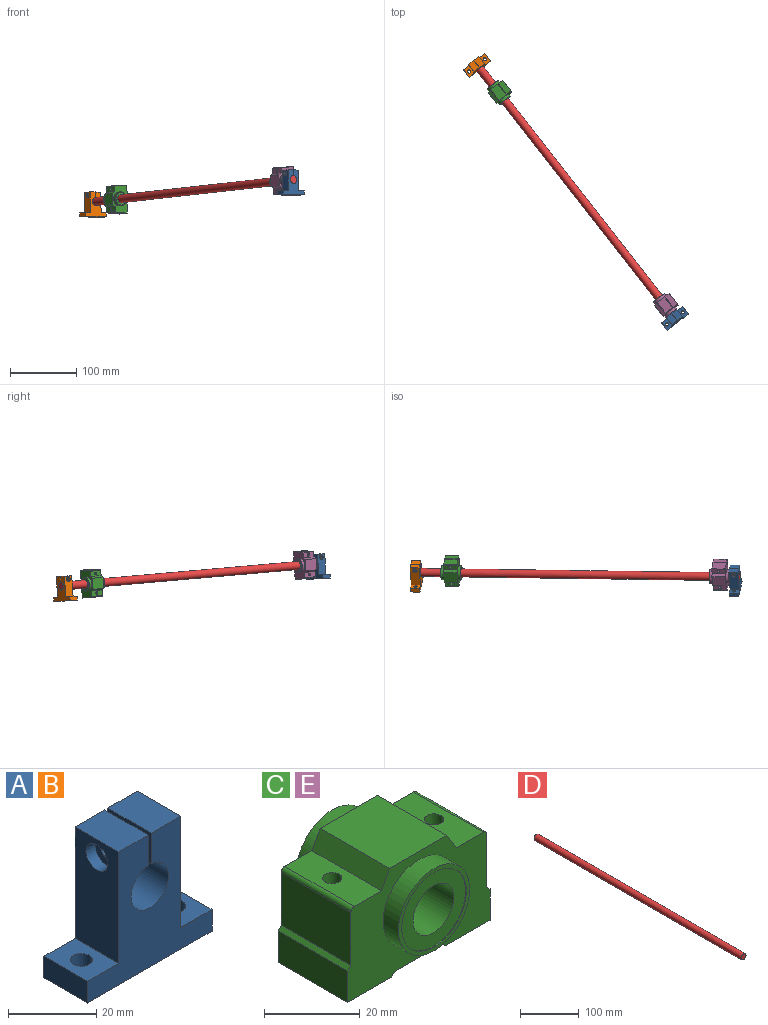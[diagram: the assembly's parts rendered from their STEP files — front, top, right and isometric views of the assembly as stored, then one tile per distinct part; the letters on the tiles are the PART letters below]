
ASSEMBLY  parts=5 mates=4
PART A: 20 faces, bbox 40x14x37 mm
  f0: plane 14x10mm, normal (0,0,1), area 120.4mm2, adj f1,f11,f12,f13,f15
  f1: plane 31x14mm, normal (1,0,0), area 426.9mm2, adj f0,f2,f12,f13,f19
  f2: plane 14x9.5mm, normal (0,0,1), area 133mm2, adj f1,f3,f12,f13
  f3: plane 14x8.52mm, normal (-1,0,0), area 112.2mm2, adj f2,f4,f12,f13,f19
  f4: cylinder r=6mm len=14mm, axis (0,1,0), area 513.8mm2, adj f3,f5,f12,f13
  f5: plane 14x8.52mm, normal (1,0,0), area 112.2mm2, adj f4,f6,f12,f13,f18
  f6: plane 14x9.5mm, normal (0,0,1), area 133mm2, adj f5,f7,f12,f13
  f7: plane 31x14mm, normal (-1,0,0), area 395.5mm2, adj f6,f8,f12,f13,f16
  f8: plane 14x10mm, normal (0,0,1), area 120.4mm2, adj f7,f9,f12,f13,f14
  f9: plane 14x6mm, normal (-1,0,0), area 84mm2, adj f8,f10,f12,f13
  f10: plane 40x14mm, normal (0,0,-1), area 520.7mm2, adj f9,f11,f12,f13,f14,f15
  f11: plane 14x6mm, normal (1,0,0), area 84mm2, adj f0,f10,f12,f13
  f12: plane 40x37mm, normal (0,-1,0), area 738.4mm2, adj f0,f1,f2,f3,f4,f5,f6,f7
  f13: plane 40x37mm, normal (0,1,0), area 738.4mm2, adj f0,f1,f2,f3,f4,f5,f6,f7
  f14: cylinder r=2.5mm len=6mm, axis (0,0,1), area 94.2mm2, adj f8,f10
  f15: cylinder r=2.5mm len=6mm, axis (0,0,1), area 94.2mm2, adj f0,f10
  f16: cylinder r=3.5mm len=7mm, axis (-1,0,0), area 66mm2, adj f7,f17
  f17: plane 7x7mm, normal (-1,0,0), area 31.4mm2, adj f16,f18
  f18: cylinder r=1.5mm len=6.5mm, axis (-1,0,0), area 61.3mm2, adj f5,f17
  f19: cylinder r=1.5mm len=9.5mm, axis (-1,0,0), area 89.5mm2, adj f1,f3
PART B: same geometry as A
PART C: 31 faces, bbox 42x30x28 mm
  f0: cylinder r=9.5mm len=19mm, axis (0,1,0), area 11.9mm2, adj f25,f28
  f1: plane 20.5x14mm, normal (0,0,-1), area 287mm2, adj f2,f18,f19,f20
  f2: plane 20.5x1mm, normal (-0.71,0,-0.71), area 29mm2, adj f1,f3,f19,f20
  f3: plane 20.5x13mm, normal (0,0,-1), area 253.9mm2, adj f2,f4,f19,f20,f30
  f4: plane 20.5x8mm, normal (1,0,0), area 164mm2, adj f3,f5,f19,f20
  f5: plane 20.5x1mm, normal (0.71,0,0.71), area 29mm2, adj f4,f6,f19,f20
  f6: plane 20.5x13.5mm, normal (1,0,0), area 276.7mm2, adj f5,f7,f19,f20
  f7: cylinder r=1mm len=20.5mm, axis (0,1,0), area 32.2mm2, adj f6,f8,f19,f20
  f8: plane 20.5x8mm, normal (0,0,1), area 151.4mm2, adj f7,f9,f19,f20,f30
  f9: plane 20.5x4.5mm, normal (0.86,0,0.51), area 107.5mm2, adj f8,f10,f19,f20
  f10: plane 20.5x16.89mm, normal (0,0,1), area 346.2mm2, adj f9,f11,f19,f20
  f11: plane 20.5x4.5mm, normal (-0.88,0,0.47), area 104.7mm2, adj f10,f12,f19,f20
  f12: plane 20.5x8mm, normal (0,0,1), area 151.4mm2, adj f11,f13,f19,f20,f29
  f13: cylinder r=1mm len=20.5mm, axis (0,1,0), area 32.2mm2, adj f12,f14,f19,f20
  f14: plane 20.5x13.5mm, normal (-1,0,0), area 276.7mm2, adj f13,f15,f19,f20
  f15: plane 20.5x1mm, normal (-0.71,0,0.71), area 29mm2, adj f14,f16,f19,f20
  f16: plane 20.5x8mm, normal (-1,0,0), area 164mm2, adj f15,f17,f19,f20
  f17: plane 20.5x13mm, normal (0,0,-1), area 253.9mm2, adj f16,f18,f19,f20,f29
  f18: plane 20.5x1mm, normal (0.71,0,-0.71), area 29mm2, adj f1,f17,f19,f20
  f19: plane 42x28mm, normal (0,-1,0), area 682.7mm2, adj f1,f2,f3,f4,f5,f6,f7,f8
  f20: plane 42x28mm, normal (0,1,0), area 682.7mm2, adj f1,f2,f3,f4,f5,f6,f7,f8
  f21: cylinder r=10.5mm len=21mm, axis (0,1,0), area 329.9mm2, adj f20,f25
  f22: cylinder r=9.5mm len=19mm, axis (0,1,0), area 11.9mm2, adj f24,f27
  f23: cylinder r=10.5mm len=21mm, axis (0,1,0), area 296.9mm2, adj f19,f24
  f24: plane 21x21mm, normal (0,-1,0), area 62.8mm2, adj f22,f23
  f25: plane 21x21mm, normal (0,1,0), area 62.8mm2, adj f0,f21
  f26: cylinder r=6mm len=29.6mm, axis (0,1,0), area 1115.9mm2, adj f27,f28
  f27: plane 19x19mm, normal (0,-1,0), area 170.4mm2, adj f22,f26
  f28: plane 19x19mm, normal (0,1,0), area 170.4mm2, adj f0,f26
  f29: cylinder r=2mm len=23.5mm, axis (0,0,1), area 295.3mm2, adj f12,f17
  f30: cylinder r=2mm len=23.5mm, axis (0,0,1), area 295.3mm2, adj f3,f8
PART D: 3 faces, bbox 12x500x12 mm
  f0: cylinder r=6mm len=500mm, axis (0,1,0), area 18849.6mm2, adj f1,f2
  f1: plane 12x12mm, normal (0,-1,0), area 113.1mm2, adj f0
  f2: plane 12x12mm, normal (0,1,0), area 113.1mm2, adj f0
PART E: same geometry as C
PLACE A rot(axis=(-0.11,0,0.99),38.2deg) t=(171.73,-636.81,24.37)mm
PLACE B rot(axis=(-0.11,0,0.99),38.2deg) t=(-126.96,-254.88,-8.99)mm
PLACE C rot(axis=(0.27,-0.9,0.34),96.1deg) t=(-135.34,-322.86,33.61)mm
PLACE D rot(axis=(-0.11,0,0.99),38.2deg) t=(-190.83,-303.23,9.37)mm
PLACE E rot(axis=(0.27,-0.9,0.34),96.1deg) t=(116.03,-644.28,61.69)mm
MATE cylindrical E.f0 <-> D.f0  axis (-0.61,0.79,-0.07) through (107.24,-684.38,42.66)mm
MATE fastened A.f4 <-> D.f0  axis (-0.61,0.79,-0.07) through (116.46,-696.16,43.69)mm
MATE cylindrical C.f0 <-> D.f0  axis (-0.61,0.79,-0.07) through (-144.13,-362.96,14.58)mm
MATE fastened B.f4 <-> D.f0  axis (-0.61,0.79,-0.07) through (-190.83,-303.23,9.37)mm
